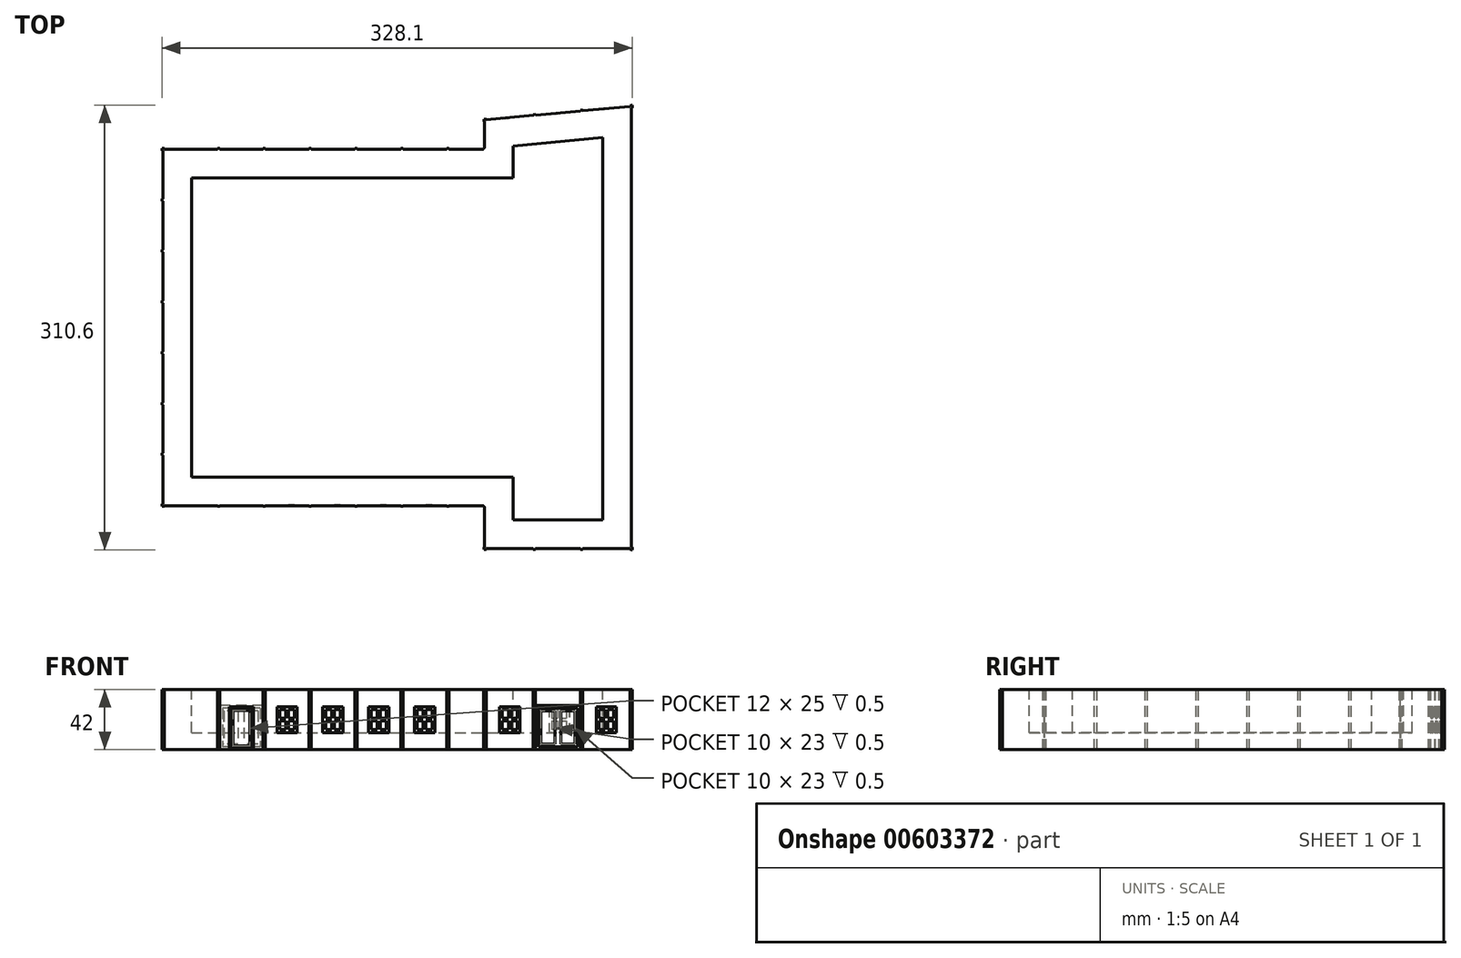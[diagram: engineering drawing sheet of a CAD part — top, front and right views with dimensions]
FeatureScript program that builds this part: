
annotation { "Feature Type Name" : "Feature", "Feature Type Description" : "" }
export const myFeature = defineFeature(function(context is Context, id is Id, definition is map)
    precondition{}
    {
        {
            var Q0;
            Q0=qCreatedBy(makeId("Top.planeOp"),FACE);
            var sketch = newSketch(context, id + "F0", { "sketchPlane" : qUnion([Q0])});
            skLineSegment(sketch, "E0", {"start": v(-327.3, -140.86) * mm, "end": v(-102.6, -140.86) * mm});
            skLineSegment(sketch, "E1", {"start": v(-102.6, -140.86) * mm, "end": v(-102.6, -170.86) * mm});
            skLineSegment(sketch, "E2", {"start": v(-102.6, -170.86) * mm, "end": v(0, -170.86) * mm});
            skLineSegment(sketch, "E3", {"start": v(0, -170.86) * mm, "end": v(0, -140.86) * mm});
            skLineSegment(sketch, "E4", {"start": v(0, 108.14) * mm, "end": v(0, 138.14) * mm});
            skLineSegment(sketch, "E5", {"start": v(-102.6, 128.64) * mm, "end": v(-102.6, 108.14) * mm});
            skLineSegment(sketch, "E6", {"start": v(-102.6, 108.14) * mm, "end": v(-327.3, 108.14) * mm});
            skLineSegment(sketch, "E7", {"start": v(-327.3, 108.14) * mm, "end": v(-327.3, -140.86) * mm});
            skLineSegment(sketch, "E8", {"start": v(-102.6, 128.64) * mm, "end": v(0, 138.14) * mm});
            skLineSegment(sketch, "E9", {"start": v(0, 108.14) * mm, "end": v(0, -140.86) * mm});
            skSolve(sketch);
        }
        {
            var Q0;
            Q0=makeQuery(id+"F0.imprint","IMPRINT",FACE,{"disambiguationData":[TD([[makeQuery(id+"F0.imprint","IMPRINT",EDGE,{"derivedFrom":sQuery(id+"F0.wireOp",EDGE,"E0")}),1.0]])]});
            extrude(context, id + "F1", {"entities" : qUnion([Q0]), "depth" : 42 * mm, "offsetDistance" : 25 * mm});
        }
        {
            var Q0;
            Q0=makeQuery(id+"F16.boolean.opBoolean","MERGE",FACE,{"derivedFrom":[makeQuery(id+"F15.boolean.opBoolean","MERGE",FACE,{"derivedFrom":[makeQuery(id+"F14.boolean.opBoolean","MERGE",FACE,{"derivedFrom":[makeQuery(id+"F13.boolean.opBoolean","MERGE",FACE,{"derivedFrom":[makeQuery(id+"F1.opExtrude","CAP_FACE",FACE,{"disambiguationData":[OSD([sQuery(id+"F0.wireOp",EDGE,"E0"),sQuery(id+"F0.wireOp",EDGE,"E1"),sQuery(id+"F0.wireOp",EDGE,"E2"),sQuery(id+"F0.wireOp",EDGE,"E3"),sQuery(id+"F0.wireOp",EDGE,"nyGmqrap-atEf-rk3b-T5WS-Qnh1Nx333F8D"),sQuery(id+"F0.wireOp",EDGE,"qoz06gKX-VQpG-udlU-9p6r-Dn6JFM5M2HmH"),sQuery(id+"F0.wireOp",EDGE,"obKySQlM-m7Bw-ihbj-WCJl-8Ek9duicwwVD"),sQuery(id+"F0.wireOp",EDGE,"E4"),sQuery(id+"F0.wireOp",EDGE,"E5"),sQuery(id+"F0.wireOp",EDGE,"E6"),sQuery(id+"F0.wireOp",EDGE,"E7"),sQuery(id+"F0.wireOp",EDGE,"E8")])],"isStart":false}),makeQuery(id+"F13.opExtrude","SWEPT_FACE",FACE,{"disambiguationData":[OSD([sQuery(id+"F4.wireOp",EDGE,"E24.bottom")])]}),makeQuery(id+"F13.opExtrude","SWEPT_FACE",FACE,{"disambiguationData":[OSD([sQuery(id+"F4.wireOp",EDGE,"E25.bottom")])]}),makeQuery(id+"F13.opExtrude","SWEPT_FACE",FACE,{"disambiguationData":[OSD([sQuery(id+"F4.wireOp",EDGE,"E26.bottom")])]}),makeQuery(id+"F13.opExtrude","SWEPT_FACE",FACE,{"disambiguationData":[OSD([sQuery(id+"F4.wireOp",EDGE,"E27.bottom")])]}),makeQuery(id+"F13.opExtrude","SWEPT_FACE",FACE,{"disambiguationData":[OSD([sQuery(id+"F4.wireOp",EDGE,"E28.bottom")])]}),makeQuery(id+"F13.opExtrude","SWEPT_FACE",FACE,{"disambiguationData":[OSD([sQuery(id+"F4.wireOp",EDGE,"E29.bottom")])]}),makeQuery(id+"F13.opExtrude","SWEPT_FACE",FACE,{"disambiguationData":[OSD([sQuery(id+"F4.wireOp",EDGE,"E30.bottom")])]}),makeQuery(id+"F13.opExtrude","SWEPT_FACE",FACE,{"disambiguationData":[OSD([sQuery(id+"F4.wireOp",EDGE,"E32.bottom")])]}),makeQuery(id+"F13.opExtrude","SWEPT_FACE",FACE,{"disambiguationData":[OSD([sQuery(id+"F6.wireOp",EDGE,"E38.bottom")])]}),makeQuery(id+"F13.opExtrude","SWEPT_FACE",FACE,{"disambiguationData":[OSD([sQuery(id+"F6.wireOp",EDGE,"E39.bottom")])]}),makeQuery(id+"F13.opExtrude","SWEPT_FACE",FACE,{"disambiguationData":[OSD([sQuery(id+"F6.wireOp",EDGE,"E45.bottom")])]}),makeQuery(id+"F13.opExtrude","SWEPT_FACE",FACE,{"disambiguationData":[OSD([sQuery(id+"F6.wireOp",EDGE,"E46.bottom")])]}),makeQuery(id+"F13.opExtrude","SWEPT_FACE",FACE,{"disambiguationData":[OSD([sQuery(id+"FZdEnrKlhhno9Gi_1.wireOp",EDGE,"KYNqBLLi-1AJf-sFVm-lYJS-7ksvNQeMZq25.bottom")])]}),makeQuery(id+"F13.opExtrude","SWEPT_FACE",FACE,{"disambiguationData":[OSD([sQuery(id+"FZdEnrKlhhno9Gi_1.wireOp",EDGE,"zW9ccelF-Ij3j-XEa1-GmtA-9e4srnjb6IXw.bottom")])]}),makeQuery(id+"F13.opExtrude","SWEPT_FACE",FACE,{"disambiguationData":[OSD([sQuery(id+"FZdEnrKlhhno9Gi_1.wireOp",EDGE,"f4c9f5db-6f29-4c17-9655-4a537888013a.1.0.1")])]}),makeQuery(id+"F13.opExtrude","SWEPT_FACE",FACE,{"disambiguationData":[OSD([sQuery(id+"FZdEnrKlhhno9Gi_1.wireOp",EDGE,"f4c9f5db-6f29-4c17-9655-4a537888013a.2.0.1")])]}),makeQuery(id+"F13.opExtrude","SWEPT_FACE",FACE,{"disambiguationData":[OSD([sQuery(id+"FZdEnrKlhhno9Gi_1.wireOp",EDGE,"f4c9f5db-6f29-4c17-9655-4a537888013a.3.0.1")])]}),makeQuery(id+"F13.opExtrude","SWEPT_FACE",FACE,{"disambiguationData":[OSD([sQuery(id+"FZdEnrKlhhno9Gi_1.wireOp",EDGE,"f4c9f5db-6f29-4c17-9655-4a537888013a.4.0.1")])]}),makeQuery(id+"F13.opExtrude","SWEPT_FACE",FACE,{"disambiguationData":[OSD([sQuery(id+"FZdEnrKlhhno9Gi_1.wireOp",EDGE,"f4c9f5db-6f29-4c17-9655-4a537888013a.5.0.1")])]}),makeQuery(id+"F13.opExtrude","SWEPT_FACE",FACE,{"disambiguationData":[OSD([sQuery(id+"FZdEnrKlhhno9Gi_1.wireOp",EDGE,"f4c9f5db-6f29-4c17-9655-4a537888013a.6.0.1")])]}),makeQuery(id+"F13.opExtrude","SWEPT_FACE",FACE,{"disambiguationData":[OSD([sQuery(id+"FZdEnrKlhhno9Gi_1.wireOp",EDGE,"f4c9f5db-6f29-4c17-9655-4a537888013a.7.0.1")])]}),makeQuery(id+"F13.opExtrude","SWEPT_FACE",FACE,{"disambiguationData":[OSD([sQuery(id+"FZdEnrKlhhno9Gi_1.wireOp",EDGE,"GeyjAZNO-VAi6-rHZs-A2eS-vhpcfcaCoKY1.bottom")])]})]}),makeQuery(id+"F14.opExtrude","SWEPT_FACE",FACE,{"disambiguationData":[OSD([sQuery(id+"F5.wireOp",EDGE,"E33.bottom")])]}),makeQuery(id+"F14.opExtrude","SWEPT_FACE",FACE,{"disambiguationData":[OSD([sQuery(id+"F5.wireOp",EDGE,"E35.bottom")])]}),makeQuery(id+"F14.opExtrude","SWEPT_FACE",FACE,{"disambiguationData":[OSD([sQuery(id+"F8.wireOp",EDGE,"E51.bottom")])]}),makeQuery(id+"F14.opExtrude","SWEPT_FACE",FACE,{"disambiguationData":[OSD([sQuery(id+"F8.wireOp",EDGE,"E52.1.0.1")])]}),makeQuery(id+"F14.opExtrude","SWEPT_FACE",FACE,{"disambiguationData":[OSD([sQuery(id+"F8.wireOp",EDGE,"E52.2.0.1")])]}),makeQuery(id+"F14.opExtrude","SWEPT_FACE",FACE,{"disambiguationData":[OSD([sQuery(id+"F8.wireOp",EDGE,"E52.3.0.1")])]}),makeQuery(id+"F14.opExtrude","SWEPT_FACE",FACE,{"disambiguationData":[OSD([sQuery(id+"F8.wireOp",EDGE,"E52.4.0.1")])]}),makeQuery(id+"F14.opExtrude","SWEPT_FACE",FACE,{"disambiguationData":[OSD([sQuery(id+"F8.wireOp",EDGE,"E52.5.0.1")])]}),makeQuery(id+"F14.opExtrude","SWEPT_FACE",FACE,{"disambiguationData":[OSD([sQuery(id+"F8.wireOp",EDGE,"E52.6.0.1")])]}),makeQuery(id+"F14.opExtrude","SWEPT_FACE",FACE,{"disambiguationData":[OSD([sQuery(id+"F8.wireOp",EDGE,"E52.7.0.1")])]}),makeQuery(id+"F14.opExtrude","SWEPT_FACE",FACE,{"disambiguationData":[OSD([sQuery(id+"F8.wireOp",EDGE,"E52.8.0.1")])]}),makeQuery(id+"F14.opExtrude","SWEPT_FACE",FACE,{"disambiguationData":[OSD([sQuery(id+"F10.wireOp",EDGE,"E74.bottom")])]}),makeQuery(id+"F14.opExtrude","SWEPT_FACE",FACE,{"disambiguationData":[OSD([sQuery(id+"F10.wireOp",EDGE,"E76.bottom")])]})]}),makeQuery(id+"F15.opExtrude","SWEPT_FACE",FACE,{"disambiguationData":[OSD([sQuery(id+"F7.wireOp",EDGE,"E47.bottom")])]}),makeQuery(id+"F15.opExtrude","SWEPT_FACE",FACE,{"disambiguationData":[OSD([sQuery(id+"F7.wireOp",EDGE,"E49.bottom")])]}),makeQuery(id+"F15.opExtrude","SWEPT_FACE",FACE,{"disambiguationData":[OSD([sQuery(id+"F89PRT1MlmpoyuR_1.wireOp",EDGE,"oPr6eM8E-15xU-sSh5-ggam-Pqrmq8a6gogU.bottom")])]}),makeQuery(id+"F15.opExtrude","SWEPT_FACE",FACE,{"disambiguationData":[OSD([sQuery(id+"F89PRT1MlmpoyuR_1.wireOp",EDGE,"5ebfc829-4a8a-400a-bbed-cf0e74b3c437.1.0.1")])]}),makeQuery(id+"F15.opExtrude","SWEPT_FACE",FACE,{"disambiguationData":[OSD([sQuery(id+"F89PRT1MlmpoyuR_1.wireOp",EDGE,"5ebfc829-4a8a-400a-bbed-cf0e74b3c437.2.0.1")])]}),makeQuery(id+"F15.opExtrude","SWEPT_FACE",FACE,{"disambiguationData":[OSD([sQuery(id+"F89PRT1MlmpoyuR_1.wireOp",EDGE,"5ebfc829-4a8a-400a-bbed-cf0e74b3c437.3.0.1")])]}),makeQuery(id+"F15.opExtrude","SWEPT_FACE",FACE,{"disambiguationData":[OSD([sQuery(id+"F89PRT1MlmpoyuR_1.wireOp",EDGE,"5ebfc829-4a8a-400a-bbed-cf0e74b3c437.4.0.1")])]}),makeQuery(id+"F15.opExtrude","SWEPT_FACE",FACE,{"disambiguationData":[OSD([sQuery(id+"F89PRT1MlmpoyuR_1.wireOp",EDGE,"5ebfc829-4a8a-400a-bbed-cf0e74b3c437.5.0.1")])]}),makeQuery(id+"F15.opExtrude","SWEPT_FACE",FACE,{"disambiguationData":[OSD([sQuery(id+"F89PRT1MlmpoyuR_1.wireOp",EDGE,"5ebfc829-4a8a-400a-bbed-cf0e74b3c437.6.0.1")])]}),makeQuery(id+"F15.opExtrude","SWEPT_FACE",FACE,{"disambiguationData":[OSD([sQuery(id+"F89PRT1MlmpoyuR_1.wireOp",EDGE,"5ebfc829-4a8a-400a-bbed-cf0e74b3c437.7.0.1")])]}),makeQuery(id+"F15.opExtrude","SWEPT_FACE",FACE,{"disambiguationData":[OSD([sQuery(id+"F89PRT1MlmpoyuR_1.wireOp",EDGE,"5ebfc829-4a8a-400a-bbed-cf0e74b3c437.8.0.1")])]}),makeQuery(id+"F15.opExtrude","SWEPT_FACE",FACE,{"disambiguationData":[OSD([sQuery(id+"F12.wireOp",EDGE,"E88.bottom")])]}),makeQuery(id+"F15.opExtrude","SWEPT_FACE",FACE,{"disambiguationData":[OSD([sQuery(id+"F12.wireOp",EDGE,"E90.bottom")])]})]}),makeQuery(id+"F16.opExtrude","SWEPT_FACE",FACE,{"disambiguationData":[OSD([sQuery(id+"F9.wireOp",EDGE,"E65.top")])]}),makeQuery(id+"F16.opExtrude","SWEPT_FACE",FACE,{"disambiguationData":[OSD([sQuery(id+"F9.wireOp",EDGE,"E66.top")])]}),makeQuery(id+"F16.opExtrude","SWEPT_FACE",FACE,{"disambiguationData":[OSD([sQuery(id+"F9.wireOp",EDGE,"E67.top")])]}),makeQuery(id+"F16.opExtrude","SWEPT_FACE",FACE,{"disambiguationData":[OSD([sQuery(id+"F9.wireOp",EDGE,"E68.top")])]}),makeQuery(id+"F16.opExtrude","SWEPT_FACE",FACE,{"disambiguationData":[OSD([sQuery(id+"F9.wireOp",EDGE,"E69.top")])]}),makeQuery(id+"F16.opExtrude","SWEPT_FACE",FACE,{"disambiguationData":[OSD([sQuery(id+"F9.wireOp",EDGE,"E70.top")])]}),makeQuery(id+"F16.opExtrude","SWEPT_FACE",FACE,{"disambiguationData":[OSD([sQuery(id+"F9.wireOp",EDGE,"E71.top")])]}),makeQuery(id+"F16.opExtrude","SWEPT_FACE",FACE,{"disambiguationData":[OSD([sQuery(id+"F9.wireOp",EDGE,"E73.top")])]}),makeQuery(id+"F16.opExtrude","SWEPT_FACE",FACE,{"disambiguationData":[OSD([sQuery(id+"F11.wireOp",EDGE,"E79.bottom")])]}),makeQuery(id+"F16.opExtrude","SWEPT_FACE",FACE,{"disambiguationData":[OSD([sQuery(id+"F11.wireOp",EDGE,"E80.bottom")])]}),makeQuery(id+"F16.opExtrude","SWEPT_FACE",FACE,{"disambiguationData":[OSD([sQuery(id+"F11.wireOp",EDGE,"E86.bottom")])]}),makeQuery(id+"F16.opExtrude","SWEPT_FACE",FACE,{"disambiguationData":[OSD([sQuery(id+"F11.wireOp",EDGE,"E87.bottom")])]}),makeQuery(id+"F16.opExtrude","SWEPT_FACE",FACE,{"disambiguationData":[OSD([sQuery(id+"F5yESZNjpBfSFAY_1.wireOp",EDGE,"4544ebec-b435-4efe-9974-cae89348029b.top")])]}),makeQuery(id+"F16.opExtrude","SWEPT_FACE",FACE,{"disambiguationData":[OSD([sQuery(id+"F5yESZNjpBfSFAY_1.wireOp",EDGE,"341fc88d-3161-4d98-8537-e2d19d3be95e.top")])]}),makeQuery(id+"F16.opExtrude","SWEPT_FACE",FACE,{"disambiguationData":[OSD([sQuery(id+"F5yESZNjpBfSFAY_1.wireOp",EDGE,"705f42c0-06a2-427d-ae09-582b00b97250.1.0.3")])]}),makeQuery(id+"F16.opExtrude","SWEPT_FACE",FACE,{"disambiguationData":[OSD([sQuery(id+"F5yESZNjpBfSFAY_1.wireOp",EDGE,"705f42c0-06a2-427d-ae09-582b00b97250.2.0.3")])]}),makeQuery(id+"F16.opExtrude","SWEPT_FACE",FACE,{"disambiguationData":[OSD([sQuery(id+"F5yESZNjpBfSFAY_1.wireOp",EDGE,"705f42c0-06a2-427d-ae09-582b00b97250.3.0.3")])]}),makeQuery(id+"F16.opExtrude","SWEPT_FACE",FACE,{"disambiguationData":[OSD([sQuery(id+"F5yESZNjpBfSFAY_1.wireOp",EDGE,"705f42c0-06a2-427d-ae09-582b00b97250.4.0.3")])]}),makeQuery(id+"F16.opExtrude","SWEPT_FACE",FACE,{"disambiguationData":[OSD([sQuery(id+"F5yESZNjpBfSFAY_1.wireOp",EDGE,"705f42c0-06a2-427d-ae09-582b00b97250.5.0.3")])]}),makeQuery(id+"F16.opExtrude","SWEPT_FACE",FACE,{"disambiguationData":[OSD([sQuery(id+"F5yESZNjpBfSFAY_1.wireOp",EDGE,"705f42c0-06a2-427d-ae09-582b00b97250.6.0.3")])]}),makeQuery(id+"F16.opExtrude","SWEPT_FACE",FACE,{"disambiguationData":[OSD([sQuery(id+"F5yESZNjpBfSFAY_1.wireOp",EDGE,"705f42c0-06a2-427d-ae09-582b00b97250.7.0.3")])]}),makeQuery(id+"F16.opExtrude","SWEPT_FACE",FACE,{"disambiguationData":[OSD([sQuery(id+"F5yESZNjpBfSFAY_1.wireOp",EDGE,"defa02a1-c160-4513-977d-9f6b6ed9877b.top")])]})]});
            var sketch = newSketch(context, id + "F2", { "sketchPlane" : qUnion([Q0])});
            skLineSegment(sketch, "E10.0", {"start": v(-20, 116.2) * mm, "end": v(-82.6, 110.4) * mm});
            skLineSegment(sketch, "E10.1", {"start": v(-82.6, -120.86) * mm, "end": v(-82.6, -150.86) * mm});
            skLineSegment(sketch, "E10.2", {"start": v(-307.3, -120.86) * mm, "end": v(-82.6, -120.86) * mm});
            skLineSegment(sketch, "E10.3", {"start": v(-307.3, 88.14) * mm, "end": v(-307.3, -120.86) * mm});
            skLineSegment(sketch, "E10.4", {"start": v(-82.6, 88.14) * mm, "end": v(-307.3, 88.14) * mm});
            skLineSegment(sketch, "E10.5", {"start": v(-82.6, -150.86) * mm, "end": v(-20, -150.86) * mm});
            skLineSegment(sketch, "E10.6", {"start": v(-82.6, 110.4) * mm, "end": v(-82.6, 88.14) * mm});
            skLineSegment(sketch, "E10.7", {"start": v(-20, -150.86) * mm, "end": v(-20, -120.86) * mm});
            skLineSegment(sketch, "E10.11", {"start": v(-20, 88.14) * mm, "end": v(-20, 116.2) * mm});
            skLineSegment(sketch, "E11", {"start": v(-20, 88.14) * mm, "end": v(-20, -120.86) * mm});
            skSolve(sketch);
        }
        {
            var Q0;
            Q0=makeQuery(id+"F2.imprint","IMPRINT",FACE,{"disambiguationData":[TD([[makeQuery(id+"F2.imprint","IMPRINT",EDGE,{"derivedFrom":sQuery(id+"F2.wireOp",EDGE,"E10.0")}),1.0]])]});
            extrude(context, id + "F3", {"entities" : qUnion([Q0]), "operationType" : NewBodyOperationType.REMOVE, "oppositeDirection" : true, "depth" : 30 * mm, "offsetDistance" : 25 * mm});
        }
        {
            var Q0;
            Q0=makeQuery(id+"F1.opExtrude","SWEPT_FACE",FACE,{"disambiguationData":[OSD([sQuery(id+"F0.wireOp",EDGE,"E0")])]});
            var sketch = newSketch(context, id + "F4", { "sketchPlane" : qUnion([Q0])});
            skPoint(sketch, "E12", {"position": v(-288.38, 0) * mm});
            skPoint(sketch, "E13", {"position": v(-256.38, 0) * mm});
            skPoint(sketch, "E14", {"position": v(-224.38, 0) * mm});
            skPoint(sketch, "E15", {"position": v(-192.38, 0) * mm});
            skPoint(sketch, "E16", {"position": v(-160.38, 0) * mm});
            skPoint(sketch, "E17", {"position": v(-128.38, 0) * mm});
            skLineSegment(sketch, "E18", {"start": v(-288.38, 42) * mm, "end": v(-288.38, -18.35) * mm, "construction": true});
            skLineSegment(sketch, "E19", {"start": v(-256.38, 42) * mm, "end": v(-256.38, 0) * mm, "construction": true});
            skLineSegment(sketch, "E20", {"start": v(-224.38, 42) * mm, "end": v(-224.38, 0) * mm, "construction": true});
            skLineSegment(sketch, "E21", {"start": v(-192.38, 42) * mm, "end": v(-192.38, 0) * mm, "construction": true});
            skLineSegment(sketch, "E22", {"start": v(-160.38, 42) * mm, "end": v(-160.38, 0) * mm, "construction": true});
            skLineSegment(sketch, "E23", {"start": v(-128.38, 42) * mm, "end": v(-128.38, 0) * mm, "construction": true});
            skLineSegment(sketch, "E24.bottom", {"start": v(-289.18, 42) * mm, "end": v(-287.58, 42) * mm});
            skLineSegment(sketch, "E24.top", {"start": v(-289.18, 0) * mm, "end": v(-287.58, 0) * mm});
            skLineSegment(sketch, "E24.left", {"start": v(-289.18, 42) * mm, "end": v(-289.18, 0) * mm});
            skLineSegment(sketch, "E24.right", {"start": v(-287.58, 42) * mm, "end": v(-287.58, 0) * mm});
            skLineSegment(sketch, "E25.bottom", {"start": v(-257.18, 42) * mm, "end": v(-255.57, 42) * mm});
            skLineSegment(sketch, "E25.top", {"start": v(-257.18, 0) * mm, "end": v(-255.57, 0) * mm});
            skLineSegment(sketch, "E25.left", {"start": v(-257.18, 42) * mm, "end": v(-257.18, 0) * mm});
            skLineSegment(sketch, "E25.right", {"start": v(-255.57, 42) * mm, "end": v(-255.57, 0) * mm});
            skLineSegment(sketch, "E26.bottom", {"start": v(-225.18, 42) * mm, "end": v(-223.58, 42) * mm});
            skLineSegment(sketch, "E26.top", {"start": v(-225.18, 0) * mm, "end": v(-223.57, 0) * mm});
            skLineSegment(sketch, "E26.left", {"start": v(-225.18, 42) * mm, "end": v(-225.18, 0) * mm});
            skLineSegment(sketch, "E26.right", {"start": v(-223.58, 42) * mm, "end": v(-223.58, 0) * mm});
            skLineSegment(sketch, "E27.bottom", {"start": v(-193.18, 42) * mm, "end": v(-191.58, 42) * mm});
            skLineSegment(sketch, "E27.top", {"start": v(-193.18, 0) * mm, "end": v(-191.57, 0) * mm});
            skLineSegment(sketch, "E27.left", {"start": v(-193.18, 42) * mm, "end": v(-193.18, 0) * mm});
            skLineSegment(sketch, "E27.right", {"start": v(-191.58, 42) * mm, "end": v(-191.58, 0) * mm});
            skLineSegment(sketch, "E28.bottom", {"start": v(-161.18, 42) * mm, "end": v(-159.58, 42) * mm});
            skLineSegment(sketch, "E28.top", {"start": v(-161.18, 0) * mm, "end": v(-159.58, 0) * mm});
            skLineSegment(sketch, "E28.left", {"start": v(-161.18, 42) * mm, "end": v(-161.18, 0) * mm});
            skLineSegment(sketch, "E28.right", {"start": v(-159.58, 42) * mm, "end": v(-159.58, 0) * mm});
            skLineSegment(sketch, "E29.bottom", {"start": v(-129.18, 42) * mm, "end": v(-127.58, 42) * mm});
            skLineSegment(sketch, "E29.top", {"start": v(-129.18, 0) * mm, "end": v(-127.58, 0) * mm});
            skLineSegment(sketch, "E29.left", {"start": v(-129.18, 42) * mm, "end": v(-129.18, 0) * mm});
            skLineSegment(sketch, "E29.right", {"start": v(-127.58, 42) * mm, "end": v(-127.58, 0) * mm});
            skLineSegment(sketch, "E30.bottom", {"start": v(-102.6, 42) * mm, "end": v(-103.4, 42) * mm});
            skLineSegment(sketch, "E30.top", {"start": v(-102.6, 0) * mm, "end": v(-103.4, 0) * mm});
            skLineSegment(sketch, "E30.left", {"start": v(-102.6, 42) * mm, "end": v(-102.6, 0) * mm});
            skLineSegment(sketch, "E30.right", {"start": v(-103.4, 42) * mm, "end": v(-103.4, 0) * mm});
            skPoint(sketch, "E31", {"position": v(-326.1, 42) * mm});
            skLineSegment(sketch, "E32.bottom", {"start": v(-326.1, 42) * mm, "end": v(-327.7, 42) * mm});
            skLineSegment(sketch, "E32.top", {"start": v(-326.1, 0) * mm, "end": v(-327.7, 0) * mm});
            skLineSegment(sketch, "E32.left", {"start": v(-326.1, 42) * mm, "end": v(-326.1, 0) * mm});
            skLineSegment(sketch, "E32.right", {"start": v(-327.7, 42) * mm, "end": v(-327.7, 0) * mm});
            skSolve(sketch);
        }
        {
            var Q0;
            Q0=makeQuery(id+"F1.opExtrude","SWEPT_FACE",FACE,{"disambiguationData":[OSD([sQuery(id+"F0.wireOp",EDGE,"E1")])]});
            var sketch = newSketch(context, id + "F5", { "sketchPlane" : qUnion([Q0])});
            skLineSegment(sketch, "E33.bottom", {"start": v(140.86, 42) * mm, "end": v(141.66, 42) * mm});
            skLineSegment(sketch, "E33.top", {"start": v(140.86, 0) * mm, "end": v(141.66, 0) * mm});
            skLineSegment(sketch, "E33.left", {"start": v(140.86, 42) * mm, "end": v(140.86, 0) * mm});
            skLineSegment(sketch, "E33.right", {"start": v(141.66, 42) * mm, "end": v(141.66, 0) * mm});
            skPoint(sketch, "E34", {"position": v(169.66, 42) * mm});
            skLineSegment(sketch, "E35.bottom", {"start": v(169.66, 42) * mm, "end": v(171.26, 42) * mm});
            skLineSegment(sketch, "E35.top", {"start": v(169.66, 0) * mm, "end": v(171.26, 0) * mm});
            skLineSegment(sketch, "E35.left", {"start": v(169.66, 42) * mm, "end": v(169.66, 0) * mm});
            skLineSegment(sketch, "E35.right", {"start": v(171.26, 42) * mm, "end": v(171.26, 0) * mm});
            skSolve(sketch);
        }
        {
            var Q0;
            Q0=makeQuery(id+"F1.opExtrude","SWEPT_FACE",FACE,{"disambiguationData":[OSD([sQuery(id+"F0.wireOp",EDGE,"E2")])]});
            var sketch = newSketch(context, id + "F6", { "sketchPlane" : qUnion([Q0])});
            skPoint(sketch, "E36", {"position": v(-101.4, 42) * mm});
            skPoint(sketch, "E37", {"position": v(-1.2, 42) * mm});
            skLineSegment(sketch, "E38.bottom", {"start": v(-101.4, 42) * mm, "end": v(-103, 42) * mm});
            skLineSegment(sketch, "E38.top", {"start": v(-101.4, 0) * mm, "end": v(-103, 0) * mm});
            skLineSegment(sketch, "E38.left", {"start": v(-101.4, 42) * mm, "end": v(-101.4, 0) * mm});
            skLineSegment(sketch, "E38.right", {"start": v(-103, 42) * mm, "end": v(-103, 0) * mm});
            skLineSegment(sketch, "E39.bottom", {"start": v(-1.2, 42) * mm, "end": v(0.4, 42) * mm});
            skLineSegment(sketch, "E39.top", {"start": v(-1.2, 0) * mm, "end": v(0.4, 0) * mm});
            skLineSegment(sketch, "E39.left", {"start": v(-1.2, 42) * mm, "end": v(-1.2, 0) * mm});
            skLineSegment(sketch, "E39.right", {"start": v(0.4, 42) * mm, "end": v(0.4, 0) * mm});
            skPoint(sketch, "E40", {"position": v(-51.3, 42) * mm});
            skPoint(sketch, "E41", {"position": v(-51.3, 0) * mm});
            skLineSegment(sketch, "E42", {"start": v(-51.3, 42) * mm, "end": v(-51.3, 0) * mm, "construction": true});
            skPoint(sketch, "E43", {"position": v(-67.8, 42) * mm});
            skPoint(sketch, "E44", {"position": v(-34.8, 42) * mm});
            skLineSegment(sketch, "E45.bottom", {"start": v(-35.6, 42) * mm, "end": v(-34, 42) * mm});
            skLineSegment(sketch, "E45.top", {"start": v(-35.6, 0) * mm, "end": v(-34, 0) * mm});
            skLineSegment(sketch, "E45.left", {"start": v(-35.6, 42) * mm, "end": v(-35.6, 0) * mm});
            skLineSegment(sketch, "E45.right", {"start": v(-34, 42) * mm, "end": v(-34, 0) * mm});
            skLineSegment(sketch, "E46.bottom", {"start": v(-68.6, 42) * mm, "end": v(-67, 42) * mm});
            skLineSegment(sketch, "E46.top", {"start": v(-68.6, 0) * mm, "end": v(-67, 0) * mm});
            skLineSegment(sketch, "E46.left", {"start": v(-68.6, 42) * mm, "end": v(-68.6, 0) * mm});
            skLineSegment(sketch, "E46.right", {"start": v(-67, 42) * mm, "end": v(-67, 0) * mm});
            skSolve(sketch);
        }
        {
            var Q0;
            Q0=makeQuery(id+"F1.opExtrude","SWEPT_FACE",FACE,{"disambiguationData":[OSD([sQuery(id+"F0.wireOp",EDGE,"E3")])]});
            var sketch = newSketch(context, id + "F7", { "sketchPlane" : qUnion([Q0])});
            skLineSegment(sketch, "E47.bottom", {"start": v(-170.86, 42) * mm, "end": v(-171.66, 42) * mm});
            skLineSegment(sketch, "E47.top", {"start": v(-170.86, 0) * mm, "end": v(-171.66, 0) * mm});
            skLineSegment(sketch, "E47.left", {"start": v(-170.86, 42) * mm, "end": v(-170.86, 0) * mm});
            skLineSegment(sketch, "E47.right", {"start": v(-171.66, 42) * mm, "end": v(-171.66, 0) * mm});
            skPoint(sketch, "E48", {"position": v(-169.66, 42) * mm});
            skLineSegment(sketch, "E49.bottom", {"start": v(-169.66, 42) * mm, "end": v(-171.26, 42) * mm});
            skLineSegment(sketch, "E49.top", {"start": v(-169.66, 0) * mm, "end": v(-171.26, 0) * mm});
            skLineSegment(sketch, "E49.left", {"start": v(-169.66, 42) * mm, "end": v(-169.66, 0) * mm});
            skLineSegment(sketch, "E49.right", {"start": v(-171.26, 42) * mm, "end": v(-171.26, 0) * mm});
            skSolve(sketch);
        }
        {
            var Q0;
            Q0=makeQuery(id+"F1.opExtrude","SWEPT_FACE",FACE,{"disambiguationData":[OSD([sQuery(id+"F0.wireOp",EDGE,"E7")])]});
            var sketch = newSketch(context, id + "F8", { "sketchPlane" : qUnion([Q0])});
            skPoint(sketch, "E50", {"position": v(-107.24, 42) * mm});
            skLineSegment(sketch, "E51.bottom", {"start": v(-107.24, 42) * mm, "end": v(-108.84, 42) * mm});
            skLineSegment(sketch, "E51.top", {"start": v(-107.24, 0) * mm, "end": v(-108.84, 0) * mm});
            skLineSegment(sketch, "E51.left", {"start": v(-107.24, 42) * mm, "end": v(-107.24, 0) * mm});
            skLineSegment(sketch, "E51.right", {"start": v(-108.84, 42) * mm, "end": v(-108.84, 0) * mm});
            skLineSegment(sketch, "E52.1.0.0", {"start": v(-71.74, 42) * mm, "end": v(-71.74, 0) * mm});
            skLineSegment(sketch, "E52.1.0.1", {"start": v(-71.74, 42) * mm, "end": v(-73.34, 42) * mm});
            skLineSegment(sketch, "E52.1.0.2", {"start": v(-73.34, 42) * mm, "end": v(-73.34, 0) * mm});
            skLineSegment(sketch, "E52.1.0.3", {"start": v(-71.74, 0) * mm, "end": v(-73.34, 0) * mm});
            skLineSegment(sketch, "E52.2.0.0", {"start": v(-36.24, 42) * mm, "end": v(-36.24, 0) * mm});
            skLineSegment(sketch, "E52.2.0.1", {"start": v(-36.24, 42) * mm, "end": v(-37.84, 42) * mm});
            skLineSegment(sketch, "E52.2.0.2", {"start": v(-37.84, 42) * mm, "end": v(-37.84, 0) * mm});
            skLineSegment(sketch, "E52.2.0.3", {"start": v(-36.24, 0) * mm, "end": v(-37.84, 0) * mm});
            skLineSegment(sketch, "E52.3.0.0", {"start": v(-0.74, 42) * mm, "end": v(-0.74, 0) * mm});
            skLineSegment(sketch, "E52.3.0.1", {"start": v(-0.74, 42) * mm, "end": v(-2.34, 42) * mm});
            skLineSegment(sketch, "E52.3.0.2", {"start": v(-2.34, 42) * mm, "end": v(-2.34, 0) * mm});
            skLineSegment(sketch, "E52.3.0.3", {"start": v(-0.74, 0) * mm, "end": v(-2.34, 0) * mm});
            skLineSegment(sketch, "E52.4.0.0", {"start": v(34.76, 42) * mm, "end": v(34.76, 0) * mm});
            skLineSegment(sketch, "E52.4.0.1", {"start": v(34.76, 42) * mm, "end": v(33.16, 42) * mm});
            skLineSegment(sketch, "E52.4.0.2", {"start": v(33.16, 42) * mm, "end": v(33.16, 0) * mm});
            skLineSegment(sketch, "E52.4.0.3", {"start": v(34.76, 0) * mm, "end": v(33.16, 0) * mm});
            skLineSegment(sketch, "E52.5.0.0", {"start": v(70.26, 42) * mm, "end": v(70.26, 0) * mm});
            skLineSegment(sketch, "E52.5.0.1", {"start": v(70.26, 42) * mm, "end": v(68.66, 42) * mm});
            skLineSegment(sketch, "E52.5.0.2", {"start": v(68.66, 42) * mm, "end": v(68.66, 0) * mm});
            skLineSegment(sketch, "E52.5.0.3", {"start": v(70.26, 0) * mm, "end": v(68.66, 0) * mm});
            skLineSegment(sketch, "E52.6.0.0", {"start": v(105.76, 42) * mm, "end": v(105.76, 0) * mm});
            skLineSegment(sketch, "E52.6.0.1", {"start": v(105.76, 42) * mm, "end": v(104.16, 42) * mm});
            skLineSegment(sketch, "E52.6.0.2", {"start": v(104.16, 42) * mm, "end": v(104.16, 0) * mm});
            skLineSegment(sketch, "E52.6.0.3", {"start": v(105.76, 0) * mm, "end": v(104.16, 0) * mm});
            skLineSegment(sketch, "E52.7.0.0", {"start": v(141.26, 42) * mm, "end": v(141.26, 0) * mm});
            skLineSegment(sketch, "E52.7.0.1", {"start": v(141.26, 42) * mm, "end": v(139.66, 42) * mm});
            skLineSegment(sketch, "E52.7.0.2", {"start": v(139.66, 42) * mm, "end": v(139.66, 0) * mm});
            skLineSegment(sketch, "E52.7.0.3", {"start": v(141.26, 0) * mm, "end": v(139.66, 0) * mm});
            skLineSegment(sketch, "E52.direction1", {"start": v(-107.24, 0) * mm, "end": v(-71.74, 0) * mm, "construction": true});
            skSolve(sketch);
        }
        {
            var Q0;
            Q0=makeQuery(id+"F1.opExtrude","SWEPT_FACE",FACE,{"disambiguationData":[OSD([sQuery(id+"F0.wireOp",EDGE,"E6")])]});
            var sketch = newSketch(context, id + "F9", { "sketchPlane" : qUnion([Q0])});
            skPoint(sketch, "E53", {"position": v(288.38, 51.7) * mm});
            skPoint(sketch, "E54", {"position": v(256.38, 51.7) * mm});
            skPoint(sketch, "E55", {"position": v(224.38, 51.7) * mm});
            skPoint(sketch, "E56", {"position": v(192.38, 51.7) * mm});
            skPoint(sketch, "E57", {"position": v(160.38, 51.7) * mm});
            skPoint(sketch, "E58", {"position": v(128.38, 51.7) * mm});
            skLineSegment(sketch, "E59", {"start": v(288.38, 0) * mm, "end": v(288.38, 70.05) * mm, "construction": true});
            skLineSegment(sketch, "E60", {"start": v(256.38, 0) * mm, "end": v(256.38, 51.7) * mm, "construction": true});
            skLineSegment(sketch, "E61", {"start": v(224.38, 0) * mm, "end": v(224.38, 51.7) * mm, "construction": true});
            skLineSegment(sketch, "E62", {"start": v(192.38, 0) * mm, "end": v(192.38, 51.7) * mm, "construction": true});
            skLineSegment(sketch, "E63", {"start": v(160.38, 0) * mm, "end": v(160.38, 51.7) * mm, "construction": true});
            skLineSegment(sketch, "E64", {"start": v(128.38, 0) * mm, "end": v(128.38, 51.7) * mm, "construction": true});
            skLineSegment(sketch, "E65.bottom", {"start": v(289.18, 0) * mm, "end": v(287.58, 0) * mm});
            skLineSegment(sketch, "E65.top", {"start": v(289.18, 42) * mm, "end": v(287.58, 42) * mm});
            skLineSegment(sketch, "E65.left", {"start": v(289.18, 0) * mm, "end": v(289.18, 42) * mm});
            skLineSegment(sketch, "E65.right", {"start": v(287.58, 0) * mm, "end": v(287.58, 42) * mm});
            skLineSegment(sketch, "E66.bottom", {"start": v(257.18, 0) * mm, "end": v(255.57, 0) * mm});
            skLineSegment(sketch, "E66.top", {"start": v(257.18, 42) * mm, "end": v(255.57, 42) * mm});
            skLineSegment(sketch, "E66.left", {"start": v(257.18, 0) * mm, "end": v(257.18, 42) * mm});
            skLineSegment(sketch, "E66.right", {"start": v(255.57, 0) * mm, "end": v(255.57, 42) * mm});
            skLineSegment(sketch, "E67.bottom", {"start": v(225.18, 0) * mm, "end": v(223.58, 0) * mm});
            skLineSegment(sketch, "E67.top", {"start": v(225.18, 42) * mm, "end": v(223.58, 42) * mm});
            skLineSegment(sketch, "E67.left", {"start": v(225.18, 0) * mm, "end": v(225.18, 42) * mm});
            skLineSegment(sketch, "E67.right", {"start": v(223.58, 0) * mm, "end": v(223.58, 42) * mm});
            skLineSegment(sketch, "E68.bottom", {"start": v(193.18, 0) * mm, "end": v(191.58, 0) * mm});
            skLineSegment(sketch, "E68.top", {"start": v(193.18, 42) * mm, "end": v(191.58, 42) * mm});
            skLineSegment(sketch, "E68.left", {"start": v(193.18, 0) * mm, "end": v(193.18, 42) * mm});
            skLineSegment(sketch, "E68.right", {"start": v(191.58, 0) * mm, "end": v(191.58, 42) * mm});
            skLineSegment(sketch, "E69.bottom", {"start": v(161.18, 0) * mm, "end": v(159.58, 0) * mm});
            skLineSegment(sketch, "E69.top", {"start": v(161.18, 42) * mm, "end": v(159.58, 42) * mm});
            skLineSegment(sketch, "E69.left", {"start": v(161.18, 0) * mm, "end": v(161.18, 42) * mm});
            skLineSegment(sketch, "E69.right", {"start": v(159.58, 0) * mm, "end": v(159.58, 42) * mm});
            skLineSegment(sketch, "E70.bottom", {"start": v(129.18, 0) * mm, "end": v(127.58, 0) * mm});
            skLineSegment(sketch, "E70.top", {"start": v(129.18, 42) * mm, "end": v(127.58, 42) * mm});
            skLineSegment(sketch, "E70.left", {"start": v(129.18, 0) * mm, "end": v(129.18, 42) * mm});
            skLineSegment(sketch, "E70.right", {"start": v(127.58, 0) * mm, "end": v(127.58, 42) * mm});
            skLineSegment(sketch, "E71.bottom", {"start": v(102.6, 0) * mm, "end": v(103.4, 0) * mm});
            skLineSegment(sketch, "E71.top", {"start": v(102.6, 42) * mm, "end": v(103.4, 42) * mm});
            skLineSegment(sketch, "E71.left", {"start": v(102.6, 0) * mm, "end": v(102.6, 42) * mm});
            skLineSegment(sketch, "E71.right", {"start": v(103.4, 0) * mm, "end": v(103.4, 42) * mm});
            skPoint(sketch, "E72", {"position": v(326.1, 0) * mm});
            skLineSegment(sketch, "E73.bottom", {"start": v(326.1, 0) * mm, "end": v(327.7, 0) * mm});
            skLineSegment(sketch, "E73.top", {"start": v(326.1, 42) * mm, "end": v(327.7, 42) * mm});
            skLineSegment(sketch, "E73.left", {"start": v(326.1, 0) * mm, "end": v(326.1, 42) * mm});
            skLineSegment(sketch, "E73.right", {"start": v(327.7, 0) * mm, "end": v(327.7, 42) * mm});
            skSolve(sketch);
        }
        {
            var Q0;
            Q0=makeQuery(id+"F1.opExtrude","SWEPT_FACE",FACE,{"disambiguationData":[OSD([sQuery(id+"F0.wireOp",EDGE,"E5")])]});
            var sketch = newSketch(context, id + "F10", { "sketchPlane" : qUnion([Q0])});
            skLineSegment(sketch, "E74.bottom", {"start": v(-108.14, 42) * mm, "end": v(-108.94, 42) * mm});
            skLineSegment(sketch, "E74.top", {"start": v(-108.14, 0) * mm, "end": v(-108.94, 0) * mm});
            skLineSegment(sketch, "E74.left", {"start": v(-108.14, 42) * mm, "end": v(-108.14, 0) * mm});
            skLineSegment(sketch, "E74.right", {"start": v(-108.94, 42) * mm, "end": v(-108.94, 0) * mm});
            skPoint(sketch, "E75", {"position": v(-127.44, 42) * mm});
            skLineSegment(sketch, "E76.bottom", {"start": v(-127.44, 42) * mm, "end": v(-129.04, 42) * mm});
            skLineSegment(sketch, "E76.top", {"start": v(-127.44, 0) * mm, "end": v(-129.04, 0) * mm});
            skLineSegment(sketch, "E76.left", {"start": v(-127.44, 42) * mm, "end": v(-127.44, 0) * mm});
            skLineSegment(sketch, "E76.right", {"start": v(-129.04, 42) * mm, "end": v(-129.04, 0) * mm});
            skSolve(sketch);
        }
        {
            var Q0;
            Q0=makeQuery(id+"F1.opExtrude","SWEPT_FACE",FACE,{"disambiguationData":[OSD([sQuery(id+"F0.wireOp",EDGE,"E8")])]});
            var sketch = newSketch(context, id + "F11", { "sketchPlane" : qUnion([Q0])});
            skPoint(sketch, "E77", {"position": v(-11.54, 42) * mm});
            skPoint(sketch, "E78", {"position": v(89.07, 42) * mm});
            skLineSegment(sketch, "E79.bottom", {"start": v(-11.54, 42) * mm, "end": v(-13.14, 42) * mm});
            skLineSegment(sketch, "E79.top", {"start": v(-11.54, 0) * mm, "end": v(-13.14, 0) * mm});
            skLineSegment(sketch, "E79.left", {"start": v(-11.54, 42) * mm, "end": v(-11.54, 0) * mm});
            skLineSegment(sketch, "E79.right", {"start": v(-13.14, 42) * mm, "end": v(-13.14, 0) * mm});
            skLineSegment(sketch, "E80.bottom", {"start": v(89.07, 42) * mm, "end": v(90.67, 42) * mm});
            skLineSegment(sketch, "E80.top", {"start": v(89.07, 0) * mm, "end": v(90.67, 0) * mm});
            skLineSegment(sketch, "E80.left", {"start": v(89.07, 42) * mm, "end": v(89.07, 0) * mm});
            skLineSegment(sketch, "E80.right", {"start": v(90.67, 42) * mm, "end": v(90.67, 0) * mm});
            skPoint(sketch, "E81", {"position": v(38.78, 42) * mm});
            skPoint(sketch, "E82", {"position": v(38.78, 0) * mm});
            skLineSegment(sketch, "E83", {"start": v(38.78, 42) * mm, "end": v(38.78, 0) * mm, "construction": true});
            skPoint(sketch, "E84", {"position": v(22.28, 42) * mm});
            skPoint(sketch, "E85", {"position": v(55.28, 42) * mm});
            skLineSegment(sketch, "E86.bottom", {"start": v(21.48, 42) * mm, "end": v(23.08, 42) * mm});
            skLineSegment(sketch, "E86.top", {"start": v(21.48, 0) * mm, "end": v(23.08, 0) * mm});
            skLineSegment(sketch, "E86.left", {"start": v(21.48, 42) * mm, "end": v(21.48, 0) * mm});
            skLineSegment(sketch, "E86.right", {"start": v(23.08, 42) * mm, "end": v(23.08, 0) * mm});
            skLineSegment(sketch, "E87.bottom", {"start": v(54.48, 42) * mm, "end": v(56.08, 42) * mm});
            skLineSegment(sketch, "E87.top", {"start": v(54.48, 0) * mm, "end": v(56.08, 0) * mm});
            skLineSegment(sketch, "E87.left", {"start": v(54.48, 42) * mm, "end": v(54.48, 0) * mm});
            skLineSegment(sketch, "E87.right", {"start": v(56.08, 42) * mm, "end": v(56.08, 0) * mm});
            skSolve(sketch);
        }
        {
            var Q0;
            Q0=makeQuery(id+"F1.opExtrude","SWEPT_FACE",FACE,{"disambiguationData":[OSD([sQuery(id+"F0.wireOp",EDGE,"E4")])]});
            var sketch = newSketch(context, id + "F12", { "sketchPlane" : qUnion([Q0])});
            skLineSegment(sketch, "E88.bottom", {"start": v(138.14, 42) * mm, "end": v(138.94, 42) * mm});
            skLineSegment(sketch, "E88.top", {"start": v(138.14, 0) * mm, "end": v(138.94, 0) * mm});
            skLineSegment(sketch, "E88.left", {"start": v(138.14, 42) * mm, "end": v(138.14, 0) * mm});
            skLineSegment(sketch, "E88.right", {"start": v(138.94, 42) * mm, "end": v(138.94, 0) * mm});
            skPoint(sketch, "E89", {"position": v(136.98, 42) * mm});
            skLineSegment(sketch, "E90.bottom", {"start": v(136.98, 42) * mm, "end": v(138.58, 42) * mm});
            skLineSegment(sketch, "E90.top", {"start": v(136.98, 0) * mm, "end": v(138.58, 0) * mm});
            skLineSegment(sketch, "E90.left", {"start": v(136.98, 42) * mm, "end": v(136.98, 0) * mm});
            skLineSegment(sketch, "E90.right", {"start": v(138.58, 42) * mm, "end": v(138.58, 0) * mm});
            skSolve(sketch);
        }
        {
            var Q0;
            Q0=qSketchRegion(id+"F4",true);
            var Q1;
            Q1=qSketchRegion(id+"F6",true);
            var Q2;
            Q2=qSketchRegion(id+"FZdEnrKlhhno9Gi_1",true);
            extrude(context, id + "F13", {"entities" : qUnion([Q0, Q1, Q2]), "operationType" : NewBodyOperationType.ADD, "depth" : .4 * mm, "offsetDistance" : 25 * mm});
        }
        {
            var Q0;
            Q0=qSketchRegion(id+"F5",true);
            var Q1;
            Q1=qSketchRegion(id+"F8",true);
            var Q2;
            Q2=qSketchRegion(id+"F10",true);
            extrude(context, id + "F14", {"entities" : qUnion([Q0, Q1, Q2]), "operationType" : NewBodyOperationType.ADD, "depth" : .4 * mm, "offsetDistance" : 25 * mm});
        }
        {
            var Q0;
            Q0=qSketchRegion(id+"F7",true);
            var Q1;
            Q1=qSketchRegion(id+"F89PRT1MlmpoyuR_1",true);
            var Q2;
            Q2=qSketchRegion(id+"F12",true);
            extrude(context, id + "F15", {"entities" : qUnion([Q0, Q1, Q2]), "operationType" : NewBodyOperationType.ADD, "depth" : .4 * mm, "offsetDistance" : 25 * mm});
        }
        {
            var Q0;
            Q0=qSketchRegion(id+"F9",true);
            var Q1;
            Q1=qSketchRegion(id+"F11",true);
            var Q2;
            Q2=qSketchRegion(id+"F5yESZNjpBfSFAY_1",true);
            extrude(context, id + "F16", {"entities" : qUnion([Q0, Q1, Q2]), "operationType" : NewBodyOperationType.ADD, "depth" : .4 * mm, "offsetDistance" : 25 * mm});
        }
        {
            var Q0;
            {var subQ9=sQuery(id+"F0.wireOp",EDGE,"E2");Q0=makeQuery(id+"F13.boolean.opBoolean","SPLIT",FACE,{"disambiguationData":[TD([makeQuery(id+"F13.opExtrude","SWEPT_FACE",FACE,{"disambiguationData":[OSD([sQuery(id+"F6.wireOp",EDGE,"E38.left")])]})])],"derivedFrom":makeQuery(id+"F1.opExtrude","SWEPT_FACE",FACE,{"disambiguationData":[OSD([subQ9])]})});}
            var sketch = newSketch(context, id + "F17", { "sketchPlane" : qUnion([Q0])});
            skLineSegment(sketch, "E91.bottom", {"start": v(-92.07, 30) * mm, "end": v(-77.93, 30) * mm});
            skLineSegment(sketch, "E91.top", {"start": v(-92.07, 12) * mm, "end": v(-77.93, 12) * mm});
            skLineSegment(sketch, "E91.left", {"start": v(-92.07, 30) * mm, "end": v(-92.07, 12) * mm});
            skLineSegment(sketch, "E91.right", {"start": v(-77.93, 30) * mm, "end": v(-77.93, 12) * mm});
            skLineSegment(sketch, "E92.0", {"start": v(-90.14, 28.07) * mm, "end": v(-85.96, 28.07) * mm});
            skLineSegment(sketch, "E92.1", {"start": v(-90.14, 28.07) * mm, "end": v(-90.14, 21.96) * mm});
            skLineSegment(sketch, "E92.2", {"start": v(-90.14, 13.93) * mm, "end": v(-85.96, 13.93) * mm});
            skLineSegment(sketch, "E92.3", {"start": v(-79.86, 28.07) * mm, "end": v(-79.86, 21.96) * mm});
            skLineSegment(sketch, "E93.left", {"start": v(-85.96, 28.07) * mm, "end": v(-85.96, 21.96) * mm});
            skLineSegment(sketch, "E93.right", {"start": v(-84.04, 28.07) * mm, "end": v(-84.04, 21.96) * mm});
            skLineSegment(sketch, "E94.bottom", {"start": v(-79.86, 21.96) * mm, "end": v(-84.04, 21.96) * mm});
            skLineSegment(sketch, "E94.top", {"start": v(-79.86, 20.04) * mm, "end": v(-84.04, 20.04) * mm});
            skLineSegment(sketch, "E95.trimOffspring", {"start": v(-85.96, 21.96) * mm, "end": v(-90.14, 21.96) * mm});
            skLineSegment(sketch, "E96.trimOffspring", {"start": v(-85.96, 20.04) * mm, "end": v(-85.96, 13.93) * mm});
            skLineSegment(sketch, "E97.trimOffspring", {"start": v(-85.96, 20.04) * mm, "end": v(-90.14, 20.04) * mm});
            skLineSegment(sketch, "E98.trimOffspring", {"start": v(-84.04, 20.04) * mm, "end": v(-84.04, 13.93) * mm});
            skLineSegment(sketch, "E99.trimOffspring", {"start": v(-79.86, 20.04) * mm, "end": v(-79.86, 13.93) * mm});
            skLineSegment(sketch, "E100.trimOffspring", {"start": v(-90.14, 20.04) * mm, "end": v(-90.14, 13.93) * mm});
            skLineSegment(sketch, "E101.trimOffspring", {"start": v(-84.04, 28.07) * mm, "end": v(-79.86, 28.07) * mm});
            skLineSegment(sketch, "E102.trimOffspring", {"start": v(-84.04, 13.93) * mm, "end": v(-79.86, 13.93) * mm});
            skSolve(sketch);
        }
        {
            var Q0;
            {var subQ9=sQuery(id+"F0.wireOp",EDGE,"E2");Q0=makeQuery(id+"F13.boolean.opBoolean","SPLIT",FACE,{"disambiguationData":[TD([makeQuery(id+"F13.opExtrude","SWEPT_FACE",FACE,{"disambiguationData":[OSD([sQuery(id+"F6.wireOp",EDGE,"E39.left")])]})])],"derivedFrom":makeQuery(id+"F1.opExtrude","SWEPT_FACE",FACE,{"disambiguationData":[OSD([subQ9])]})});}
            var sketch = newSketch(context, id + "F18", { "sketchPlane" : qUnion([Q0])});
            skLineSegment(sketch, "E103.bottom", {"start": v(-24.67, 30) * mm, "end": v(-10.53, 30) * mm});
            skLineSegment(sketch, "E103.top", {"start": v(-24.67, 12) * mm, "end": v(-10.53, 12) * mm});
            skLineSegment(sketch, "E103.left", {"start": v(-24.67, 30) * mm, "end": v(-24.67, 12) * mm});
            skLineSegment(sketch, "E103.right", {"start": v(-10.53, 30) * mm, "end": v(-10.53, 12) * mm});
            skLineSegment(sketch, "E104.0", {"start": v(-22.74, 28.07) * mm, "end": v(-18.56, 28.07) * mm});
            skLineSegment(sketch, "E104.1", {"start": v(-22.74, 28.07) * mm, "end": v(-22.74, 21.96) * mm});
            skLineSegment(sketch, "E104.2", {"start": v(-22.74, 13.93) * mm, "end": v(-18.56, 13.93) * mm});
            skLineSegment(sketch, "E104.3", {"start": v(-12.46, 28.07) * mm, "end": v(-12.46, 21.96) * mm});
            skLineSegment(sketch, "E105.left", {"start": v(-18.56, 28.07) * mm, "end": v(-18.56, 21.96) * mm});
            skLineSegment(sketch, "E105.right", {"start": v(-16.64, 28.07) * mm, "end": v(-16.64, 21.96) * mm});
            skLineSegment(sketch, "E106.bottom", {"start": v(-12.46, 21.96) * mm, "end": v(-16.64, 21.96) * mm});
            skLineSegment(sketch, "E106.top", {"start": v(-12.46, 20.04) * mm, "end": v(-16.64, 20.04) * mm});
            skLineSegment(sketch, "E107.trimOffspring", {"start": v(-18.56, 21.96) * mm, "end": v(-22.74, 21.96) * mm});
            skLineSegment(sketch, "E108.trimOffspring", {"start": v(-18.56, 20.04) * mm, "end": v(-18.56, 13.93) * mm});
            skLineSegment(sketch, "E109.trimOffspring", {"start": v(-18.56, 20.04) * mm, "end": v(-22.74, 20.04) * mm});
            skLineSegment(sketch, "E110.trimOffspring", {"start": v(-16.64, 20.04) * mm, "end": v(-16.64, 13.93) * mm});
            skLineSegment(sketch, "E111.trimOffspring", {"start": v(-12.46, 20.04) * mm, "end": v(-12.46, 13.93) * mm});
            skLineSegment(sketch, "E112.trimOffspring", {"start": v(-22.74, 20.04) * mm, "end": v(-22.74, 13.93) * mm});
            skLineSegment(sketch, "E113.trimOffspring", {"start": v(-16.64, 28.07) * mm, "end": v(-12.46, 28.07) * mm});
            skLineSegment(sketch, "E114.trimOffspring", {"start": v(-16.64, 13.93) * mm, "end": v(-12.46, 13.93) * mm});
            skSolve(sketch);
        }
        {
            var Q0;
            {var subQ11=sQuery(id+"F0.wireOp",EDGE,"E0");Q0=makeQuery(id+"F13.boolean.opBoolean","SPLIT",FACE,{"disambiguationData":[TD([makeQuery(id+"F13.opExtrude","SWEPT_FACE",FACE,{"disambiguationData":[OSD([sQuery(id+"F4.wireOp",EDGE,"E26.right")])]})])],"derivedFrom":makeQuery(id+"F1.opExtrude","SWEPT_FACE",FACE,{"disambiguationData":[OSD([subQ11])]})});}
            var sketch = newSketch(context, id + "F19", { "sketchPlane" : qUnion([Q0])});
            skLineSegment(sketch, "E115.bottom", {"start": v(-215.58, 30) * mm, "end": v(-201.43, 30) * mm});
            skLineSegment(sketch, "E115.top", {"start": v(-215.58, 12) * mm, "end": v(-201.43, 12) * mm});
            skLineSegment(sketch, "E115.left", {"start": v(-215.58, 30) * mm, "end": v(-215.58, 12) * mm});
            skLineSegment(sketch, "E115.right", {"start": v(-201.43, 30) * mm, "end": v(-201.43, 12) * mm});
            skLineSegment(sketch, "E116.0", {"start": v(-213.65, 28.07) * mm, "end": v(-209.47, 28.07) * mm});
            skLineSegment(sketch, "E116.1", {"start": v(-213.65, 28.07) * mm, "end": v(-213.65, 21.96) * mm});
            skLineSegment(sketch, "E116.2", {"start": v(-213.65, 13.93) * mm, "end": v(-209.47, 13.93) * mm});
            skLineSegment(sketch, "E116.3", {"start": v(-203.36, 28.07) * mm, "end": v(-203.36, 21.96) * mm});
            skLineSegment(sketch, "E117.left", {"start": v(-209.47, 28.07) * mm, "end": v(-209.47, 21.96) * mm});
            skLineSegment(sketch, "E117.right", {"start": v(-207.54, 28.07) * mm, "end": v(-207.54, 21.96) * mm});
            skLineSegment(sketch, "E118.bottom", {"start": v(-203.36, 21.96) * mm, "end": v(-207.54, 21.96) * mm});
            skLineSegment(sketch, "E118.top", {"start": v(-203.36, 20.04) * mm, "end": v(-207.54, 20.04) * mm});
            skLineSegment(sketch, "E119.trimOffspring", {"start": v(-209.47, 21.96) * mm, "end": v(-213.65, 21.96) * mm});
            skLineSegment(sketch, "E120.trimOffspring", {"start": v(-209.47, 20.04) * mm, "end": v(-209.47, 13.93) * mm});
            skLineSegment(sketch, "E121.trimOffspring", {"start": v(-209.47, 20.04) * mm, "end": v(-213.65, 20.04) * mm});
            skLineSegment(sketch, "E122.trimOffspring", {"start": v(-207.54, 20.04) * mm, "end": v(-207.54, 13.93) * mm});
            skLineSegment(sketch, "E123.trimOffspring", {"start": v(-203.36, 20.04) * mm, "end": v(-203.36, 13.93) * mm});
            skLineSegment(sketch, "E124.trimOffspring", {"start": v(-213.65, 20.04) * mm, "end": v(-213.65, 13.93) * mm});
            skLineSegment(sketch, "E125.trimOffspring", {"start": v(-207.54, 28.07) * mm, "end": v(-203.36, 28.07) * mm});
            skLineSegment(sketch, "E126.trimOffspring", {"start": v(-207.54, 13.93) * mm, "end": v(-203.36, 13.93) * mm});
            skSolve(sketch);
        }
        {
            var Q0;
            Q0=qSketchRegion(id+"F17",true);
            var Q1;
            Q1=qSketchRegion(id+"F18",true);
            var Q2;
            Q2=qSketchRegion(id+"F19",true);
            var Q3;
            Q3=qSketchRegion(id+"FdOBm2loh9Dp4dc_1",true);
            var Q4;
            Q4=qSketchRegion(id+"FY3zykOt8QbZdy5_1",true);
            var Q5;
            Q5=qSketchRegion(id+"FAGqtvrS7YIPi1H_1",true);
            var Q6;
            Q6=qSketchRegion(id+"FQFn3NphHTKGCZ7_1",true);
            extrude(context, id + "F20", {"entities" : qUnion([Q0, Q1, Q2, Q3, Q4, Q5, Q6]), "operationType" : NewBodyOperationType.REMOVE, "oppositeDirection" : true, "depth" : .5 * mm, "offsetDistance" : 25 * mm});
        }
        {
            var Q0;
            {var subQ11=sQuery(id+"F0.wireOp",EDGE,"E0");Q0=makeQuery(id+"F13.boolean.opBoolean","SPLIT",FACE,{"disambiguationData":[TD([makeQuery(id+"F13.opExtrude","SWEPT_FACE",FACE,{"disambiguationData":[OSD([sQuery(id+"F4.wireOp",EDGE,"E24.right")])]})])],"derivedFrom":makeQuery(id+"F1.opExtrude","SWEPT_FACE",FACE,{"disambiguationData":[OSD([subQ11])]})});}
            var sketch = newSketch(context, id + "F21", { "sketchPlane" : qUnion([Q0])});
            skLineSegment(sketch, "E127.bottom", {"start": v(-280.88, 30) * mm, "end": v(-263.88, 30) * mm});
            skLineSegment(sketch, "E127.top", {"start": v(-280.88, 0) * mm, "end": v(-263.88, 0) * mm});
            skLineSegment(sketch, "E127.left", {"start": v(-280.88, 30) * mm, "end": v(-280.88, 0) * mm});
            skLineSegment(sketch, "E127.right", {"start": v(-263.88, 30) * mm, "end": v(-263.88, 0) * mm});
            skLineSegment(sketch, "E128.0", {"start": v(-279.88, 29) * mm, "end": v(-279.88, 1) * mm});
            skLineSegment(sketch, "E128.1", {"start": v(-279.88, 29) * mm, "end": v(-264.88, 29) * mm});
            skLineSegment(sketch, "E128.2", {"start": v(-264.88, 29) * mm, "end": v(-264.88, 1) * mm});
            skLineSegment(sketch, "E128.3", {"start": v(-279.88, 1) * mm, "end": v(-264.88, 1) * mm});
            skLineSegment(sketch, "E129.0", {"start": v(-278.38, 27.5) * mm, "end": v(-278.38, 2.5) * mm});
            skLineSegment(sketch, "E129.1", {"start": v(-278.38, 27.5) * mm, "end": v(-266.38, 27.5) * mm});
            skLineSegment(sketch, "E129.2", {"start": v(-266.38, 27.5) * mm, "end": v(-266.38, 2.5) * mm});
            skLineSegment(sketch, "E129.3", {"start": v(-278.38, 2.5) * mm, "end": v(-266.38, 2.5) * mm});
            skPoint(sketch, "E130", {"position": v(-272.38, 0) * mm});
            skSolve(sketch);
        }
        {
            var Q0;
            Q0=makeQuery(id+"F21.imprint","IMPRINT",FACE,{"disambiguationData":[TD([[makeQuery(id+"F21.imprint","IMPRINT",EDGE,{"derivedFrom":sQuery(id+"F21.wireOp",EDGE,"E127.bottom")}),-1.0]])]});
            var Q1;
            Q1=makeQuery(id+"F21.imprint","IMPRINT",FACE,{"disambiguationData":[TD([[makeQuery(id+"F21.imprint","IMPRINT",EDGE,{"derivedFrom":sQuery(id+"F21.wireOp",EDGE,"E129.0")}),1.0]])]});
            extrude(context, id + "F22", {"entities" : qUnion([Q0, Q1]), "operationType" : NewBodyOperationType.REMOVE, "oppositeDirection" : true, "depth" : .5 * mm, "offsetDistance" : 25 * mm});
        }
        {
            var Q0;
            {var subQ9=sQuery(id+"F0.wireOp",EDGE,"E2");Q0=makeQuery(id+"F13.boolean.opBoolean","SPLIT",FACE,{"disambiguationData":[TD([makeQuery(id+"F13.opExtrude","SWEPT_FACE",FACE,{"disambiguationData":[OSD([sQuery(id+"F6.wireOp",EDGE,"E45.left")])]})])],"derivedFrom":makeQuery(id+"F1.opExtrude","SWEPT_FACE",FACE,{"disambiguationData":[OSD([subQ9])]})});}
            var sketch = newSketch(context, id + "F23", { "sketchPlane" : qUnion([Q0])});
            skLineSegment(sketch, "E131.bottom", {"start": v(-67, 31) * mm, "end": v(-35.6, 31) * mm});
            skLineSegment(sketch, "E131.top", {"start": v(-67, 0) * mm, "end": v(-35.6, 0) * mm});
            skLineSegment(sketch, "E131.left", {"start": v(-67, 31) * mm, "end": v(-67, 0) * mm});
            skLineSegment(sketch, "E131.right", {"start": v(-35.6, 31) * mm, "end": v(-35.6, 0) * mm});
            skLineSegment(sketch, "E132.0", {"start": v(-65, 29) * mm, "end": v(-37.6, 29) * mm});
            skLineSegment(sketch, "E132.1", {"start": v(-65, 29) * mm, "end": v(-65, 2) * mm});
            skLineSegment(sketch, "E132.2", {"start": v(-65, 2) * mm, "end": v(-37.6, 2) * mm});
            skLineSegment(sketch, "E132.3", {"start": v(-37.6, 29) * mm, "end": v(-37.6, 2) * mm});
            skLineSegment(sketch, "E133.bottom", {"start": v(-63.39, 27) * mm, "end": v(-53.39, 27) * mm});
            skLineSegment(sketch, "E133.top", {"start": v(-63.39, 4) * mm, "end": v(-53.39, 4) * mm});
            skLineSegment(sketch, "E133.left", {"start": v(-63.39, 27) * mm, "end": v(-63.39, 4) * mm});
            skLineSegment(sketch, "E133.right", {"start": v(-53.39, 27) * mm, "end": v(-53.39, 4) * mm});
            skLineSegment(sketch, "E134.bottom", {"start": v(-49.39, 27) * mm, "end": v(-39.39, 27) * mm});
            skLineSegment(sketch, "E134.top", {"start": v(-49.39, 4) * mm, "end": v(-39.39, 4) * mm});
            skLineSegment(sketch, "E134.left", {"start": v(-49.39, 27) * mm, "end": v(-49.39, 4) * mm});
            skLineSegment(sketch, "E134.right", {"start": v(-39.39, 27) * mm, "end": v(-39.39, 4) * mm});
            skSolve(sketch);
        }
        {
            var Q0;
            Q0=makeQuery(id+"F23.imprint","IMPRINT",FACE,{"disambiguationData":[TD([[makeQuery(id+"F23.imprint","IMPRINT",EDGE,{"derivedFrom":sQuery(id+"F23.wireOp",EDGE,"E131.bottom")}),-1.0]])]});
            var Q1;
            Q1=makeQuery(id+"F23.imprint","IMPRINT",FACE,{"disambiguationData":[TD([[makeQuery(id+"F23.imprint","IMPRINT",EDGE,{"derivedFrom":sQuery(id+"F23.wireOp",EDGE,"E133.bottom")}),-1.0]])]});
            var Q2;
            Q2=makeQuery(id+"F23.imprint","IMPRINT",FACE,{"disambiguationData":[TD([[makeQuery(id+"F23.imprint","IMPRINT",EDGE,{"derivedFrom":sQuery(id+"F23.wireOp",EDGE,"E134.bottom")}),-1.0]])]});
            extrude(context, id + "F24", {"entities" : qUnion([Q0, Q1, Q2]), "operationType" : NewBodyOperationType.REMOVE, "oppositeDirection" : true, "depth" : .5 * mm, "offsetDistance" : 25 * mm});
        }
        {
            var Q0;
            {var subQ0=sQuery(id+"F0.wireOp",EDGE,"E8");Q0=makeQuery(id+"F16.boolean.opBoolean","SPLIT",FACE,{"disambiguationData":[TD([makeQuery(id+"F16.opExtrude","SWEPT_FACE",FACE,{"disambiguationData":[OSD([sQuery(id+"F11.wireOp",EDGE,"E86.right")])]})])],"derivedFrom":makeQuery(id+"F1.opExtrude","SWEPT_FACE",FACE,{"disambiguationData":[OSD([subQ0])]})});}
            var sketch = newSketch(context, id + "F25", { "sketchPlane" : qUnion([Q0])});
            skLineSegment(sketch, "E135.bottom", {"start": v(30.97, 30) * mm, "end": v(45.12, 30) * mm});
            skLineSegment(sketch, "E135.top", {"start": v(30.97, 12) * mm, "end": v(45.12, 12) * mm});
            skLineSegment(sketch, "E135.left", {"start": v(30.97, 30) * mm, "end": v(30.97, 12) * mm});
            skLineSegment(sketch, "E135.right", {"start": v(45.12, 30) * mm, "end": v(45.12, 12) * mm});
            skLineSegment(sketch, "E136.0", {"start": v(32.9, 28.07) * mm, "end": v(37.08, 28.07) * mm});
            skLineSegment(sketch, "E136.1", {"start": v(32.9, 28.07) * mm, "end": v(32.9, 21.96) * mm});
            skLineSegment(sketch, "E136.2", {"start": v(32.9, 13.93) * mm, "end": v(37.08, 13.93) * mm});
            skLineSegment(sketch, "E136.3", {"start": v(43.19, 28.07) * mm, "end": v(43.19, 21.96) * mm});
            skLineSegment(sketch, "E137.left", {"start": v(37.08, 28.07) * mm, "end": v(37.08, 21.96) * mm});
            skLineSegment(sketch, "E137.right", {"start": v(39.01, 28.07) * mm, "end": v(39.01, 21.96) * mm});
            skLineSegment(sketch, "E138.bottom", {"start": v(43.19, 21.96) * mm, "end": v(39.01, 21.96) * mm});
            skLineSegment(sketch, "E138.top", {"start": v(43.19, 20.04) * mm, "end": v(39.01, 20.04) * mm});
            skLineSegment(sketch, "E139.trimOffspring", {"start": v(37.08, 21.96) * mm, "end": v(32.9, 21.96) * mm});
            skLineSegment(sketch, "E140.trimOffspring", {"start": v(37.08, 20.04) * mm, "end": v(37.08, 13.93) * mm});
            skLineSegment(sketch, "E141.trimOffspring", {"start": v(37.08, 20.04) * mm, "end": v(32.9, 20.04) * mm});
            skLineSegment(sketch, "E142.trimOffspring", {"start": v(39.01, 20.04) * mm, "end": v(39.01, 13.93) * mm});
            skLineSegment(sketch, "E143.trimOffspring", {"start": v(43.19, 20.04) * mm, "end": v(43.19, 13.93) * mm});
            skLineSegment(sketch, "E144.trimOffspring", {"start": v(32.9, 20.04) * mm, "end": v(32.9, 13.93) * mm});
            skLineSegment(sketch, "E145.trimOffspring", {"start": v(39.01, 28.07) * mm, "end": v(43.19, 28.07) * mm});
            skLineSegment(sketch, "E146.trimOffspring", {"start": v(39.01, 13.93) * mm, "end": v(43.19, 13.93) * mm});
            skLineSegment(sketch, "E147.bottom", {"start": v(-2.03, 30) * mm, "end": v(12.12, 30) * mm});
            skLineSegment(sketch, "E147.top", {"start": v(-2.03, 12) * mm, "end": v(12.12, 12) * mm});
            skLineSegment(sketch, "E147.left", {"start": v(-2.03, 30) * mm, "end": v(-2.03, 12) * mm});
            skLineSegment(sketch, "E147.right", {"start": v(12.12, 30) * mm, "end": v(12.12, 12) * mm});
            skLineSegment(sketch, "E148.0", {"start": v(-0.1, 28.07) * mm, "end": v(4.08, 28.07) * mm});
            skLineSegment(sketch, "E148.1", {"start": v(-0.1, 28.07) * mm, "end": v(-0.1, 21.96) * mm});
            skLineSegment(sketch, "E148.2", {"start": v(-0.1, 13.93) * mm, "end": v(4.08, 13.93) * mm});
            skLineSegment(sketch, "E148.3", {"start": v(10.19, 28.07) * mm, "end": v(10.19, 21.96) * mm});
            skLineSegment(sketch, "E149.left", {"start": v(4.08, 28.07) * mm, "end": v(4.08, 21.96) * mm});
            skLineSegment(sketch, "E149.right", {"start": v(6.01, 28.07) * mm, "end": v(6.01, 21.96) * mm});
            skLineSegment(sketch, "E150.bottom", {"start": v(10.19, 21.96) * mm, "end": v(6.01, 21.96) * mm});
            skLineSegment(sketch, "E150.top", {"start": v(10.19, 20.04) * mm, "end": v(6.01, 20.04) * mm});
            skLineSegment(sketch, "E151.trimOffspring", {"start": v(4.08, 21.96) * mm, "end": v(-0.1, 21.96) * mm});
            skLineSegment(sketch, "E152.trimOffspring", {"start": v(4.08, 20.04) * mm, "end": v(4.08, 13.93) * mm});
            skLineSegment(sketch, "E153.trimOffspring", {"start": v(4.08, 20.04) * mm, "end": v(-0.1, 20.04) * mm});
            skLineSegment(sketch, "E154.trimOffspring", {"start": v(6.01, 20.04) * mm, "end": v(6.01, 13.93) * mm});
            skLineSegment(sketch, "E155.trimOffspring", {"start": v(10.19, 20.04) * mm, "end": v(10.19, 13.93) * mm});
            skLineSegment(sketch, "E156.trimOffspring", {"start": v(-0.1, 20.04) * mm, "end": v(-0.1, 13.93) * mm});
            skLineSegment(sketch, "E157.trimOffspring", {"start": v(6.01, 28.07) * mm, "end": v(10.19, 28.07) * mm});
            skLineSegment(sketch, "E158.trimOffspring", {"start": v(6.01, 13.93) * mm, "end": v(10.19, 13.93) * mm});
            skLineSegment(sketch, "E159.bottom", {"start": v(65.37, 30) * mm, "end": v(79.52, 30) * mm});
            skLineSegment(sketch, "E159.top", {"start": v(65.37, 12) * mm, "end": v(79.52, 12) * mm});
            skLineSegment(sketch, "E159.left", {"start": v(65.37, 30) * mm, "end": v(65.37, 12) * mm});
            skLineSegment(sketch, "E159.right", {"start": v(79.52, 30) * mm, "end": v(79.52, 12) * mm});
            skLineSegment(sketch, "E160.0", {"start": v(67.3, 28.07) * mm, "end": v(71.48, 28.07) * mm});
            skLineSegment(sketch, "E160.1", {"start": v(67.3, 28.07) * mm, "end": v(67.3, 21.96) * mm});
            skLineSegment(sketch, "E160.2", {"start": v(67.3, 13.93) * mm, "end": v(71.48, 13.93) * mm});
            skLineSegment(sketch, "E160.3", {"start": v(77.59, 28.07) * mm, "end": v(77.59, 21.96) * mm});
            skLineSegment(sketch, "E161.left", {"start": v(71.48, 28.07) * mm, "end": v(71.48, 21.96) * mm});
            skLineSegment(sketch, "E161.right", {"start": v(73.41, 28.07) * mm, "end": v(73.41, 21.96) * mm});
            skLineSegment(sketch, "E162.bottom", {"start": v(77.59, 21.96) * mm, "end": v(73.41, 21.96) * mm});
            skLineSegment(sketch, "E162.top", {"start": v(77.59, 20.04) * mm, "end": v(73.41, 20.04) * mm});
            skLineSegment(sketch, "E163.trimOffspring", {"start": v(71.48, 21.96) * mm, "end": v(67.3, 21.96) * mm});
            skLineSegment(sketch, "E164.trimOffspring", {"start": v(71.48, 20.04) * mm, "end": v(71.48, 13.93) * mm});
            skLineSegment(sketch, "E165.trimOffspring", {"start": v(71.48, 20.04) * mm, "end": v(67.3, 20.04) * mm});
            skLineSegment(sketch, "E166.trimOffspring", {"start": v(73.41, 20.04) * mm, "end": v(73.41, 13.93) * mm});
            skLineSegment(sketch, "E167.trimOffspring", {"start": v(77.59, 20.04) * mm, "end": v(77.59, 13.93) * mm});
            skLineSegment(sketch, "E168.trimOffspring", {"start": v(67.3, 20.04) * mm, "end": v(67.3, 13.93) * mm});
            skLineSegment(sketch, "E169.trimOffspring", {"start": v(73.41, 28.07) * mm, "end": v(77.59, 28.07) * mm});
            skLineSegment(sketch, "E170.trimOffspring", {"start": v(73.41, 13.93) * mm, "end": v(77.59, 13.93) * mm});
            skSolve(sketch);
        }
        {
            var Q0;
            {var subQ2=sQuery(id+"F0.wireOp",EDGE,"E6");Q0=makeQuery(id+"F16.boolean.opBoolean","SPLIT",FACE,{"disambiguationData":[TD([makeQuery(id+"F16.opExtrude","SWEPT_FACE",FACE,{"disambiguationData":[OSD([sQuery(id+"F9.wireOp",EDGE,"E65.right")])]})])],"derivedFrom":makeQuery(id+"F1.opExtrude","SWEPT_FACE",FACE,{"disambiguationData":[OSD([subQ2])]})});}
            var sketch = newSketch(context, id + "F26", { "sketchPlane" : qUnion([Q0])});
            skLineSegment(sketch, "E171.bottom", {"start": v(257.18, 31) * mm, "end": v(287.58, 31) * mm});
            skLineSegment(sketch, "E171.top", {"start": v(257.18, 0) * mm, "end": v(287.58, 0) * mm});
            skLineSegment(sketch, "E171.left", {"start": v(257.18, 31) * mm, "end": v(257.18, 0) * mm});
            skLineSegment(sketch, "E171.right", {"start": v(287.58, 31) * mm, "end": v(287.58, 0) * mm});
            skLineSegment(sketch, "E172.0", {"start": v(259.18, 29) * mm, "end": v(285.58, 29) * mm});
            skLineSegment(sketch, "E172.1", {"start": v(259.18, 29) * mm, "end": v(259.18, 2) * mm});
            skLineSegment(sketch, "E172.2", {"start": v(259.18, 2) * mm, "end": v(285.58, 2) * mm});
            skLineSegment(sketch, "E172.3", {"start": v(285.58, 29) * mm, "end": v(285.58, 2) * mm});
            skLineSegment(sketch, "E173.bottom", {"start": v(260.79, 27) * mm, "end": v(270.79, 27) * mm});
            skLineSegment(sketch, "E173.top", {"start": v(260.79, 4) * mm, "end": v(270.79, 4) * mm});
            skLineSegment(sketch, "E173.left", {"start": v(260.79, 27) * mm, "end": v(260.79, 4) * mm});
            skLineSegment(sketch, "E173.right", {"start": v(270.79, 27) * mm, "end": v(270.79, 4) * mm});
            skLineSegment(sketch, "E174.bottom", {"start": v(274.79, 27) * mm, "end": v(284.79, 27) * mm});
            skLineSegment(sketch, "E174.top", {"start": v(274.79, 4) * mm, "end": v(284.79, 4) * mm});
            skLineSegment(sketch, "E174.left", {"start": v(274.79, 27) * mm, "end": v(274.79, 4) * mm});
            skLineSegment(sketch, "E174.right", {"start": v(284.79, 27) * mm, "end": v(284.79, 4) * mm});
            skPoint(sketch, "E175", {"position": v(272.38, 0) * mm});
            skSolve(sketch);
        }
        {
            var Q0;
            Q0=qSketchRegion(id+"FRCOmFyM6VvSc9A_1",true);
            var Q1;
            Q1=qSketchRegion(id+"F25",true);
            var Q2;
            Q2=qSketchRegion(id+"F26",true);
            var Q3;
            Q3=makeQuery(id+"F26.imprint","IMPRINT",FACE,{"disambiguationData":[TD([[makeQuery(id+"F26.imprint","IMPRINT",EDGE,{"derivedFrom":sQuery(id+"F26.wireOp",EDGE,"E173.bottom")}),-1.0]])]});
            var Q4;
            Q4=makeQuery(id+"F26.imprint","IMPRINT",FACE,{"disambiguationData":[TD([[makeQuery(id+"F26.imprint","IMPRINT",EDGE,{"derivedFrom":sQuery(id+"F26.wireOp",EDGE,"E174.bottom")}),-1.0]])]});
            extrude(context, id + "F27", {"entities" : qUnion([Q0, Q1, Q2, Q3, Q4]), "operationType" : NewBodyOperationType.REMOVE, "oppositeDirection" : true, "depth" : .5 * mm, "offsetDistance" : 25 * mm});
        }
        {
            var Q0;
            {var subQ11=sQuery(id+"F0.wireOp",EDGE,"E0");Q0=makeQuery(id+"F13.boolean.opBoolean","SPLIT",FACE,{"disambiguationData":[TD([makeQuery(id+"F13.opExtrude","SWEPT_FACE",FACE,{"disambiguationData":[OSD([sQuery(id+"F4.wireOp",EDGE,"E25.right")])]})])],"derivedFrom":makeQuery(id+"F1.opExtrude","SWEPT_FACE",FACE,{"disambiguationData":[OSD([subQ11])]})});}
            var sketch = newSketch(context, id + "F28", { "sketchPlane" : qUnion([Q0])});
            skLineSegment(sketch, "E176.bottom", {"start": v(-247.57, 30) * mm, "end": v(-233.43, 30) * mm});
            skLineSegment(sketch, "E176.top", {"start": v(-247.57, 12) * mm, "end": v(-233.43, 12) * mm});
            skLineSegment(sketch, "E176.left", {"start": v(-247.57, 30) * mm, "end": v(-247.57, 12) * mm});
            skLineSegment(sketch, "E176.right", {"start": v(-233.43, 30) * mm, "end": v(-233.43, 12) * mm});
            skLineSegment(sketch, "E177.0", {"start": v(-245.65, 28.07) * mm, "end": v(-241.47, 28.07) * mm});
            skLineSegment(sketch, "E177.1", {"start": v(-245.65, 28.07) * mm, "end": v(-245.65, 21.96) * mm});
            skLineSegment(sketch, "E177.2", {"start": v(-245.65, 13.93) * mm, "end": v(-241.47, 13.93) * mm});
            skLineSegment(sketch, "E177.3", {"start": v(-235.36, 28.07) * mm, "end": v(-235.36, 21.96) * mm});
            skLineSegment(sketch, "E178.left", {"start": v(-241.47, 28.07) * mm, "end": v(-241.47, 21.96) * mm});
            skLineSegment(sketch, "E178.right", {"start": v(-239.54, 28.07) * mm, "end": v(-239.54, 21.96) * mm});
            skLineSegment(sketch, "E179.bottom", {"start": v(-235.36, 21.96) * mm, "end": v(-239.54, 21.96) * mm});
            skLineSegment(sketch, "E179.top", {"start": v(-235.36, 20.04) * mm, "end": v(-239.54, 20.04) * mm});
            skLineSegment(sketch, "E180.trimOffspring", {"start": v(-241.47, 21.96) * mm, "end": v(-245.65, 21.96) * mm});
            skLineSegment(sketch, "E181.trimOffspring", {"start": v(-241.47, 20.04) * mm, "end": v(-241.47, 13.93) * mm});
            skLineSegment(sketch, "E182.trimOffspring", {"start": v(-241.47, 20.04) * mm, "end": v(-245.65, 20.04) * mm});
            skLineSegment(sketch, "E183.trimOffspring", {"start": v(-239.54, 20.04) * mm, "end": v(-239.54, 13.93) * mm});
            skLineSegment(sketch, "E184.trimOffspring", {"start": v(-235.36, 20.04) * mm, "end": v(-235.36, 13.93) * mm});
            skLineSegment(sketch, "E185.trimOffspring", {"start": v(-245.65, 20.04) * mm, "end": v(-245.65, 13.93) * mm});
            skLineSegment(sketch, "E186.trimOffspring", {"start": v(-239.54, 28.07) * mm, "end": v(-235.36, 28.07) * mm});
            skLineSegment(sketch, "E187.trimOffspring", {"start": v(-239.54, 13.93) * mm, "end": v(-235.36, 13.93) * mm});
            skLineSegment(sketch, "E188.left", {"start": v(-233.43, 30.72) * mm, "end": v(-233.43, 12.72) * mm});
            skLineSegment(sketch, "E189.bottom", {"start": v(-183.58, 30) * mm, "end": v(-169.43, 30) * mm});
            skLineSegment(sketch, "E189.top", {"start": v(-183.58, 12) * mm, "end": v(-169.43, 12) * mm});
            skLineSegment(sketch, "E189.left", {"start": v(-183.58, 30) * mm, "end": v(-183.58, 12) * mm});
            skLineSegment(sketch, "E189.right", {"start": v(-169.43, 30) * mm, "end": v(-169.43, 12) * mm});
            skLineSegment(sketch, "E190.0", {"start": v(-181.65, 28.07) * mm, "end": v(-177.47, 28.07) * mm});
            skLineSegment(sketch, "E190.1", {"start": v(-181.65, 28.07) * mm, "end": v(-181.65, 21.96) * mm});
            skLineSegment(sketch, "E190.2", {"start": v(-181.65, 13.93) * mm, "end": v(-177.47, 13.93) * mm});
            skLineSegment(sketch, "E190.3", {"start": v(-171.36, 28.07) * mm, "end": v(-171.36, 21.96) * mm});
            skLineSegment(sketch, "E191.left", {"start": v(-177.47, 28.07) * mm, "end": v(-177.47, 21.96) * mm});
            skLineSegment(sketch, "E191.right", {"start": v(-175.54, 28.07) * mm, "end": v(-175.54, 21.96) * mm});
            skLineSegment(sketch, "E192.bottom", {"start": v(-171.36, 21.96) * mm, "end": v(-175.54, 21.96) * mm});
            skLineSegment(sketch, "E192.top", {"start": v(-171.36, 20.04) * mm, "end": v(-175.54, 20.04) * mm});
            skLineSegment(sketch, "E193.trimOffspring", {"start": v(-177.47, 21.96) * mm, "end": v(-181.65, 21.96) * mm});
            skLineSegment(sketch, "E194.trimOffspring", {"start": v(-177.47, 20.04) * mm, "end": v(-177.47, 13.93) * mm});
            skLineSegment(sketch, "E195.trimOffspring", {"start": v(-177.47, 20.04) * mm, "end": v(-181.65, 20.04) * mm});
            skLineSegment(sketch, "E196.trimOffspring", {"start": v(-175.54, 20.04) * mm, "end": v(-175.54, 13.93) * mm});
            skLineSegment(sketch, "E197.trimOffspring", {"start": v(-171.36, 20.04) * mm, "end": v(-171.36, 13.93) * mm});
            skLineSegment(sketch, "E198.trimOffspring", {"start": v(-181.65, 20.04) * mm, "end": v(-181.65, 13.93) * mm});
            skLineSegment(sketch, "E199.trimOffspring", {"start": v(-175.54, 28.07) * mm, "end": v(-171.36, 28.07) * mm});
            skLineSegment(sketch, "E200.trimOffspring", {"start": v(-175.54, 13.93) * mm, "end": v(-171.36, 13.93) * mm});
            skLineSegment(sketch, "E201.bottom", {"start": v(-151.58, 30) * mm, "end": v(-137.43, 30) * mm});
            skLineSegment(sketch, "E201.top", {"start": v(-151.58, 12) * mm, "end": v(-137.43, 12) * mm});
            skLineSegment(sketch, "E201.left", {"start": v(-151.58, 30) * mm, "end": v(-151.58, 12) * mm});
            skLineSegment(sketch, "E201.right", {"start": v(-137.43, 30) * mm, "end": v(-137.43, 12) * mm});
            skLineSegment(sketch, "E202.0", {"start": v(-149.65, 28.07) * mm, "end": v(-145.47, 28.07) * mm});
            skLineSegment(sketch, "E202.1", {"start": v(-149.65, 28.07) * mm, "end": v(-149.65, 21.96) * mm});
            skLineSegment(sketch, "E202.2", {"start": v(-149.65, 13.93) * mm, "end": v(-145.47, 13.93) * mm});
            skLineSegment(sketch, "E202.3", {"start": v(-139.36, 28.07) * mm, "end": v(-139.36, 21.96) * mm});
            skLineSegment(sketch, "E203.left", {"start": v(-145.47, 28.07) * mm, "end": v(-145.47, 21.96) * mm});
            skLineSegment(sketch, "E203.right", {"start": v(-143.54, 28.07) * mm, "end": v(-143.54, 21.96) * mm});
            skLineSegment(sketch, "E204.bottom", {"start": v(-139.36, 21.96) * mm, "end": v(-143.54, 21.96) * mm});
            skLineSegment(sketch, "E204.top", {"start": v(-139.36, 20.04) * mm, "end": v(-143.54, 20.04) * mm});
            skLineSegment(sketch, "E205.trimOffspring", {"start": v(-145.47, 21.96) * mm, "end": v(-149.65, 21.96) * mm});
            skLineSegment(sketch, "E206.trimOffspring", {"start": v(-145.47, 20.04) * mm, "end": v(-145.47, 13.93) * mm});
            skLineSegment(sketch, "E207.trimOffspring", {"start": v(-145.47, 20.04) * mm, "end": v(-149.65, 20.04) * mm});
            skLineSegment(sketch, "E208.trimOffspring", {"start": v(-143.54, 20.04) * mm, "end": v(-143.54, 13.93) * mm});
            skLineSegment(sketch, "E209.trimOffspring", {"start": v(-139.36, 20.04) * mm, "end": v(-139.36, 13.93) * mm});
            skLineSegment(sketch, "E210.trimOffspring", {"start": v(-149.65, 20.04) * mm, "end": v(-149.65, 13.93) * mm});
            skLineSegment(sketch, "E211.trimOffspring", {"start": v(-143.54, 28.07) * mm, "end": v(-139.36, 28.07) * mm});
            skLineSegment(sketch, "E212.trimOffspring", {"start": v(-143.54, 13.93) * mm, "end": v(-139.36, 13.93) * mm});
            skLineSegment(sketch, "E213.left", {"start": v(-137.43, 30) * mm, "end": v(-137.43, 18.3) * mm});
            skSolve(sketch);
        }
        {
            var Q0;
            Q0=qSketchRegion(id+"F28",true);
            extrude(context, id + "F29", {"entities" : qUnion([Q0]), "operationType" : NewBodyOperationType.REMOVE, "oppositeDirection" : true, "depth" : .5 * mm, "offsetDistance" : 25 * mm});
        }
    });
